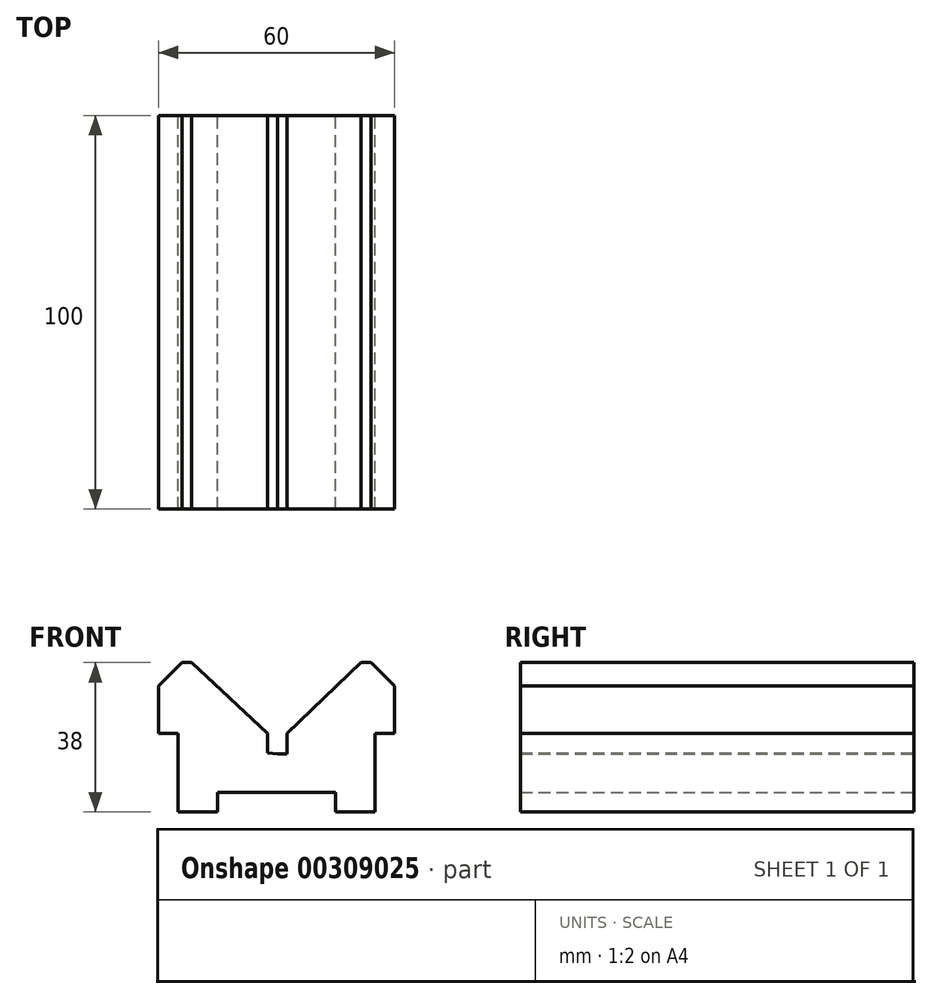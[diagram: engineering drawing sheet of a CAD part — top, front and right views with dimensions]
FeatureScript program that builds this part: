
annotation { "Feature Type Name" : "Feature", "Feature Type Description" : "" }
export const myFeature = defineFeature(function(context is Context, id is Id, definition is map)
    precondition{}
    {
        {
            var Q0;
            Q0=qCreatedBy(makeId("Front.planeOp"),FACE);
            var sketch = newSketch(context, id + "F0", { "sketchPlane" : qUnion([Q0])});
            skLineSegment(sketch, "E0", {"start": v(0, 0) * mm, "end": v(14.76, 0) * mm});
            skLineSegment(sketch, "E1", {"start": v(14.76, 0) * mm, "end": v(14.76, -5) * mm});
            skLineSegment(sketch, "E2", {"start": v(14.76, -5) * mm, "end": v(24.76, -5) * mm});
            skLineSegment(sketch, "E3", {"start": v(24.76, -5) * mm, "end": v(24.76, 15) * mm});
            skLineSegment(sketch, "E4", {"start": v(24.76, 15) * mm, "end": v(29.76, 15) * mm});
            skLineSegment(sketch, "E5", {"start": v(29.76, 15) * mm, "end": v(29.76, 27) * mm});
            skLineSegment(sketch, "E6", {"start": v(29.76, 27) * mm, "end": v(23.76, 33) * mm});
            skLineSegment(sketch, "E7", {"start": v(23.76, 33) * mm, "end": v(21.26, 33) * mm});
            skLineSegment(sketch, "E8", {"start": v(-2.5, 10) * mm, "end": v(-2.5, 15) * mm});
            skLineSegment(sketch, "E9", {"start": v(-2.5, 15) * mm, "end": v(-21.74, 33) * mm});
            skLineSegment(sketch, "E10", {"start": v(-21.74, 33) * mm, "end": v(-24.24, 33) * mm});
            skLineSegment(sketch, "E11", {"start": v(-24.24, 33) * mm, "end": v(-30.24, 27) * mm});
            skLineSegment(sketch, "E12", {"start": v(-30.24, 27) * mm, "end": v(-30.24, 15) * mm});
            skLineSegment(sketch, "E13", {"start": v(-30.24, 15) * mm, "end": v(-25.24, 15) * mm});
            skLineSegment(sketch, "E14", {"start": v(-25.24, 15) * mm, "end": v(-25.24, -5) * mm});
            skLineSegment(sketch, "E15", {"start": v(-25.24, -5) * mm, "end": v(-15.24, -5) * mm});
            skLineSegment(sketch, "E16", {"start": v(-15.24, -5) * mm, "end": v(-15.24, 0) * mm});
            skLineSegment(sketch, "E17", {"start": v(-15.24, 0) * mm, "end": v(0, 0) * mm});
            skPoint(sketch, "E18.start.orphan", {"position": v(-2.98, 15) * mm});
            skLineSegment(sketch, "E19", {"start": v(21.26, 33) * mm, "end": v(2.5, 15) * mm});
            skLineSegment(sketch, "E20", {"start": v(2.5, 15) * mm, "end": v(2.5, 9.72) * mm});
            skPoint(sketch, "E21.end.orphan", {"position": v(2.5, 10) * mm});
            skLineSegment(sketch, "E22", {"start": v(2.5, 9.72) * mm, "end": v(0, 9.72) * mm});
            skLineSegment(sketch, "E23", {"start": v(0, 9.72) * mm, "end": v(-2.5, 10) * mm});
            skSolve(sketch);
        }
        {
            var Q0;
            Q0=makeQuery(id+"F0.imprint","IMPRINT",FACE,{"disambiguationData":[TD([[makeQuery(id+"F0.imprint","IMPRINT",EDGE,{"derivedFrom":sQuery(id+"F0.wireOp",EDGE,"E0")}),1.0]])]});
            extrude(context, id + "F1", {"entities" : qUnion([Q0]), "depth" : 100 * mm});
        }
    });
